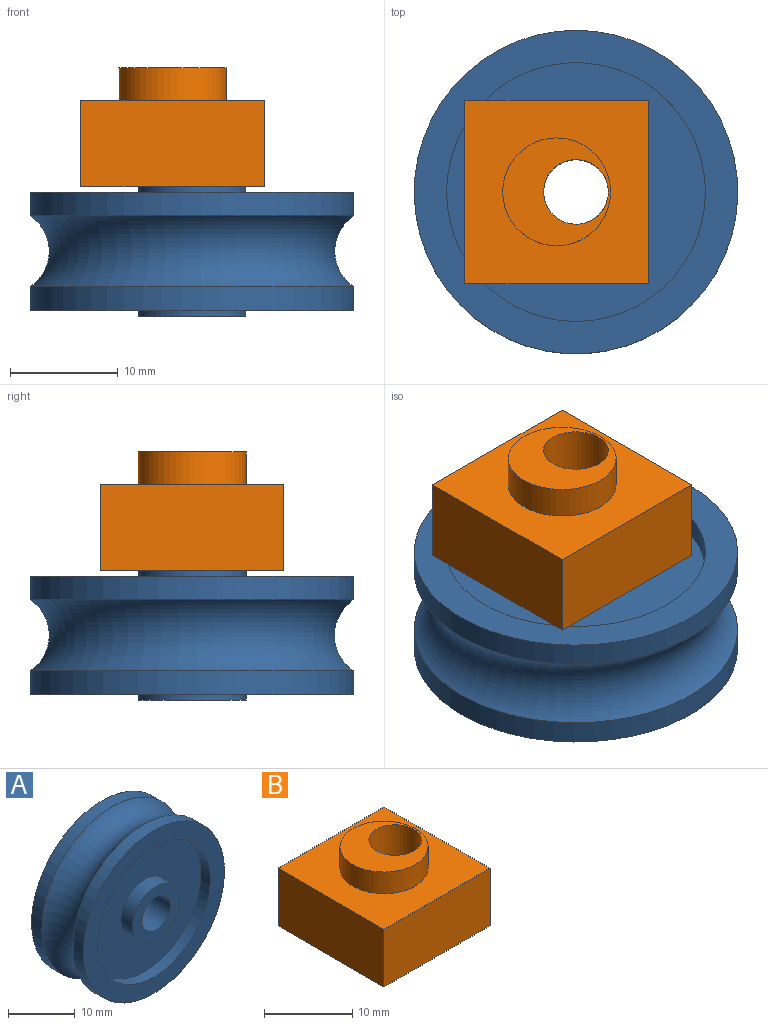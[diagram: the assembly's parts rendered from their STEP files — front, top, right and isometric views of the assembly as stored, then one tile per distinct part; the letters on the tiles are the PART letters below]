
ASSEMBLY  parts=2 mates=1
PART A: 14 faces, bbox 37.3x12x37.3 mm
  f0: torus R=17.25mm, axis (0,1,0), area 677.8mm2, adj f1,f8
  f1: cylinder r=15mm len=30mm, axis (0,1,0), area 206.7mm2, adj f0,f2
  f2: plane 30x30mm, normal (0,-1,0), area 254.5mm2, adj f1,f3
  f3: cylinder r=12mm len=24mm, axis (0,-1,0), area 150.8mm2, adj f2,f4
  f4: plane 24x24mm, normal (0,-1,0), area 373.8mm2, adj f3,f7
  f5: cylinder r=3mm len=12mm, axis (0,1,0), area 226.2mm2, adj f6,f12
  f6: plane 10x10mm, normal (0,-1,0), area 50.3mm2, adj f5,f7
  f7: cylinder r=5mm len=10mm, axis (0,1,0), area 78.5mm2, adj f4,f6
  f8: cylinder r=15mm len=30mm, axis (0,-1,0), area 206.7mm2, adj f0,f9
  f9: plane 30x30mm, normal (0,1,0), area 254.5mm2, adj f8,f10
  f10: cylinder r=12mm len=24mm, axis (0,1,0), area 150.8mm2, adj f9,f11
  f11: plane 24x24mm, normal (0,1,0), area 373.8mm2, adj f10,f13
  f12: plane 10x10mm, normal (0,1,0), area 50.3mm2, adj f5,f13
  f13: cylinder r=5mm len=10mm, axis (0,-1,0), area 78.5mm2, adj f11,f12
PART B: 9 faces, bbox 17x17x11 mm
  f0: cylinder r=3mm len=11mm, axis (0,0,-1), area 207.3mm2, adj f2,f3
  f1: cylinder r=5mm len=10mm, axis (0,0,-1), area 94.2mm2, adj f2,f8
  f2: plane 10x10mm, normal (0,0,1), area 50.3mm2, adj f0,f1
  f3: plane 17x17mm, normal (0,0,-1), area 260.7mm2, adj f0,f4,f5,f6,f7
  f4: plane 17x8mm, normal (1,0,0), area 136mm2, adj f3,f5,f7,f8
  f5: plane 17x8mm, normal (0,1,0), area 136mm2, adj f3,f4,f6,f8
  f6: plane 17x8mm, normal (-1,0,0), area 136mm2, adj f3,f5,f7,f8
  f7: plane 17x8mm, normal (0,-1,0), area 136mm2, adj f3,f4,f6,f8
  f8: plane 17x17mm, normal (0,0,1), area 210.5mm2, adj f1,f4,f5,f6,f7
PLACE A rot(axis=(-1,0,0),90deg) t=(-24.53,-11.22,-5.52)mm
PLACE B t=(3.67,-11.22,0.48)mm
MATE fastened A.f5 <-> B.f0  axis (0,0,1) through (-24.53,-11.22,0.48)mm
